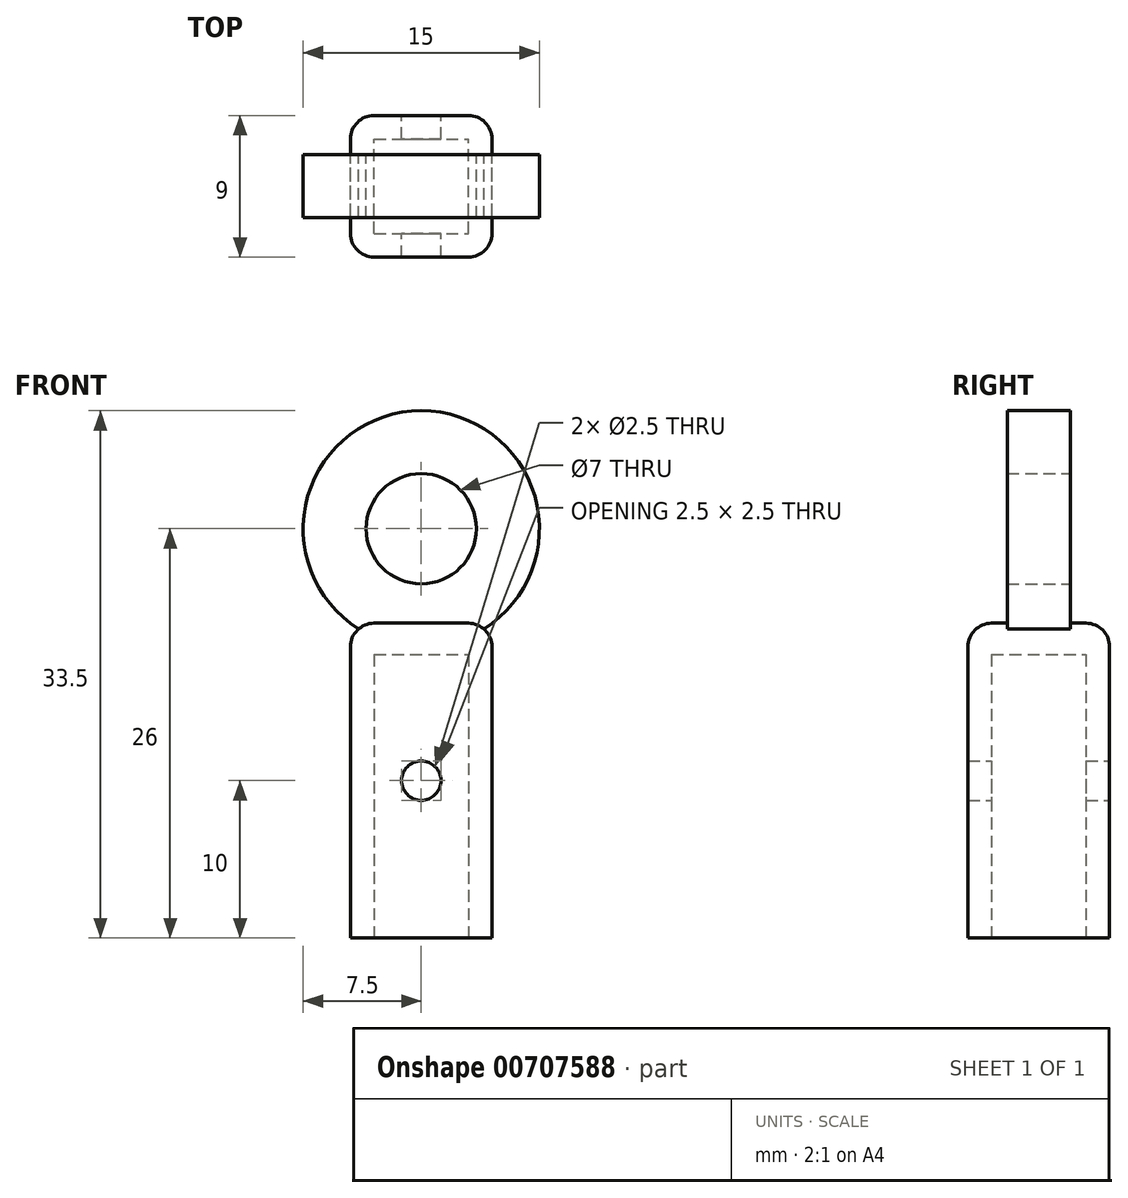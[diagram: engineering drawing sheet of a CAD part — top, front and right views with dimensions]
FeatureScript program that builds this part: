
annotation { "Feature Type Name" : "Feature", "Feature Type Description" : "" }
export const myFeature = defineFeature(function(context is Context, id is Id, definition is map)
    precondition{}
    {
        {
            var Q0;
            Q0=qCreatedBy(makeId("Top.planeOp"),FACE);
            var sketch = newSketch(context, id + "F0", { "sketchPlane" : qUnion([Q0])});
            skLineSegment(sketch, "E0.bottom", {"start": v(-3, -3) * mm, "end": v(3, -3) * mm});
            skLineSegment(sketch, "E0.top", {"start": v(-3, 3) * mm, "end": v(3, 3) * mm});
            skLineSegment(sketch, "E0.left", {"start": v(-3, -3) * mm, "end": v(-3, 3) * mm});
            skLineSegment(sketch, "E0.right", {"start": v(3, -3) * mm, "end": v(3, 3) * mm});
            skPoint(sketch, "E0.middle", {"position": v(0, 0) * mm});
            skLineSegment(sketch, "E1.bottom", {"start": v(4.5, -4.5) * mm, "end": v(-4.5, -4.5) * mm});
            skLineSegment(sketch, "E1.top", {"start": v(4.5, 4.5) * mm, "end": v(-4.5, 4.5) * mm});
            skLineSegment(sketch, "E1.left", {"start": v(4.5, -4.5) * mm, "end": v(4.5, 4.5) * mm});
            skLineSegment(sketch, "E1.right", {"start": v(-4.5, -4.5) * mm, "end": v(-4.5, 4.5) * mm});
            skSolve(sketch);
        }
        {
            var Q0;
            Q0=makeQuery(id+"F0.imprint","IMPRINT",FACE,{"disambiguationData":[TD([[makeQuery(id+"F0.imprint","IMPRINT",EDGE,{"derivedFrom":sQuery(id+"F0.wireOp",EDGE,"E0.bottom")}),-1.0]])]});
            extrude(context, id + "F1", {"entities" : qUnion([Q0]), "depth" : 20 * mm, "offsetDistance" : 25 * mm});
        }
        {
            var Q0;
            Q0=makeQuery(id+"F0.imprint","IMPRINT",FACE,{"disambiguationData":[TD([[makeQuery(id+"F0.imprint","IMPRINT",EDGE,{"derivedFrom":sQuery(id+"F0.wireOp",EDGE,"E0.bottom")}),1.0]])]});
            extrude(context, id + "F2", {"entities" : qUnion([Q0]), "operationType" : NewBodyOperationType.ADD, "depth" : 20 * mm, "offsetDistance" : 25 * mm, "hasSecondDirection" : true, "secondDirectionOppositeDirection" : false, "secondDirectionDepth" : 18 * mm});
        }
        {
            var Q0;
            Q0=makeQuery(id+"F1.opExtrude","CAP_EDGE",EDGE,{"disambiguationData":[OSD([sQuery(id+"F0.wireOp",EDGE,"E1.left")])],"isStart":false});
            var Q1;
            Q1=makeQuery(id+"F1.opExtrude","CAP_EDGE",EDGE,{"disambiguationData":[OSD([sQuery(id+"F0.wireOp",EDGE,"E1.bottom")])],"isStart":false});
            var Q2;
            Q2=makeQuery(id+"F1.opExtrude","CAP_EDGE",EDGE,{"disambiguationData":[OSD([sQuery(id+"F0.wireOp",EDGE,"E1.right")])],"isStart":false});
            var Q3;
            Q3=makeQuery(id+"F1.opExtrude","CAP_EDGE",EDGE,{"disambiguationData":[OSD([sQuery(id+"F0.wireOp",EDGE,"E1.top")])],"isStart":false});
            var Q4;
            Q4=makeQuery(id+"F1.opExtrude","SWEPT_EDGE",EDGE,{"disambiguationData":[OSD([sQuery(id+"F0.wireOp",EDGE,"E1.bottom"),sQuery(id+"F0.wireOp",EDGE,"E1.left")])]});
            var Q5;
            Q5=makeQuery(id+"F1.opExtrude","SWEPT_EDGE",EDGE,{"disambiguationData":[OSD([sQuery(id+"F0.wireOp",EDGE,"E1.top"),sQuery(id+"F0.wireOp",EDGE,"E1.left")])]});
            var Q6;
            Q6=makeQuery(id+"F1.opExtrude","SWEPT_EDGE",EDGE,{"disambiguationData":[OSD([sQuery(id+"F0.wireOp",EDGE,"E1.bottom"),sQuery(id+"F0.wireOp",EDGE,"E1.right")])]});
            var Q7;
            Q7=makeQuery(id+"F1.opExtrude","SWEPT_EDGE",EDGE,{"disambiguationData":[OSD([sQuery(id+"F0.wireOp",EDGE,"E1.top"),sQuery(id+"F0.wireOp",EDGE,"E1.right")])]});
            fillet(context, id + "F3", {"entities" : qUnion([Q0, Q1, Q2, Q3, Q4, Q5, Q6, Q7]), "radius" : 1.5 * mm, "tangentPropagation" : true, "allowEdgeOverflow" : false});
        }
        {
            var Q0;
            Q0=qCreatedBy(makeId("Front.planeOp"),FACE);
            var sketch = newSketch(context, id + "F4", { "sketchPlane" : qUnion([Q0])});
            skLineSegment(sketch, "E2", {"start": v(0, 0) * mm, "end": v(0, 20) * mm, "construction": true});
            skLineSegment(sketch, "E3", {"start": v(0, 20) * mm, "end": v(0, 26) * mm, "construction": true});
            skCircle(sketch, "E4", {"center": v(0, 26) * mm, "radius": 5.5 * mm});
            skSolve(sketch);
        }
        {
            var Q0;
            Q0=qCreatedBy(makeId("Right.planeOp"),FACE);
            var sketch = newSketch(context, id + "F5", { "sketchPlane" : qUnion([Q0])});
            skLineSegment(sketch, "E5", {"start": v(0, 0) * mm, "end": v(0, 26) * mm, "construction": true});
            skLineSegment(sketch, "E6", {"start": v(0, 26) * mm, "end": v(0, 31.5) * mm, "construction": true});
            skLineSegment(sketch, "E7.bottom", {"start": v(2, 29.5) * mm, "end": v(-2, 29.5) * mm});
            skLineSegment(sketch, "E7.top", {"start": v(2, 33.5) * mm, "end": v(-2, 33.5) * mm});
            skLineSegment(sketch, "E7.left", {"start": v(2, 29.5) * mm, "end": v(2, 33.5) * mm});
            skLineSegment(sketch, "E7.right", {"start": v(-2, 29.5) * mm, "end": v(-2, 33.5) * mm});
            skPoint(sketch, "E7.middle", {"position": v(0, 31.5) * mm});
            skPoint(sketch, "E7.cornerSnap0", {"position": v(0, 29.5) * mm});
            skSolve(sketch);
        }
        {
            var Q0;
            Q0=makeQuery(id+"F5.imprint","IMPRINT",FACE,{"disambiguationData":[TD([[makeQuery(id+"F5.imprint","IMPRINT",EDGE,{"derivedFrom":sQuery(id+"F5.wireOp",EDGE,"E7.bottom")}),-1.0]])]});
            var Q1;
            Q1=sQuery(id+"F4.wireOp",EDGE,"E4");
            revolve(context, id + "F6", {"operationType" : NewBodyOperationType.ADD, "surfaceOperationType" : NewSurfaceOperationType.NEW, "entities" : qUnion([Q0]), "axis" : qUnion([Q1]), "revolveType" : RevolveType.FULL});
        }
        {
            var Q0;
            Q0=qCreatedBy(makeId("Front.planeOp"),FACE);
            var sketch = newSketch(context, id + "F7", { "sketchPlane" : qUnion([Q0])});
            skLineSegment(sketch, "E8", {"start": v(0, 0) * mm, "end": v(0, 10) * mm, "construction": true});
            skCircle(sketch, "E9", {"center": v(0, 10) * mm, "radius": 1.25 * mm});
            skSolve(sketch);
        }
        {
            var Q0;
            Q0 = qSketchRegion(id + "F7", true);
            extrude(context, id + "F8", {"entities" : qUnion([Q0]), "operationType" : NewBodyOperationType.REMOVE, "depth" : 25 * mm, "offsetDistance" : 25 * mm, "hasSecondDirection" : true, "secondDirectionOppositeDirection" : true, "secondDirectionDepth" : 25 * mm});
        }
    });
